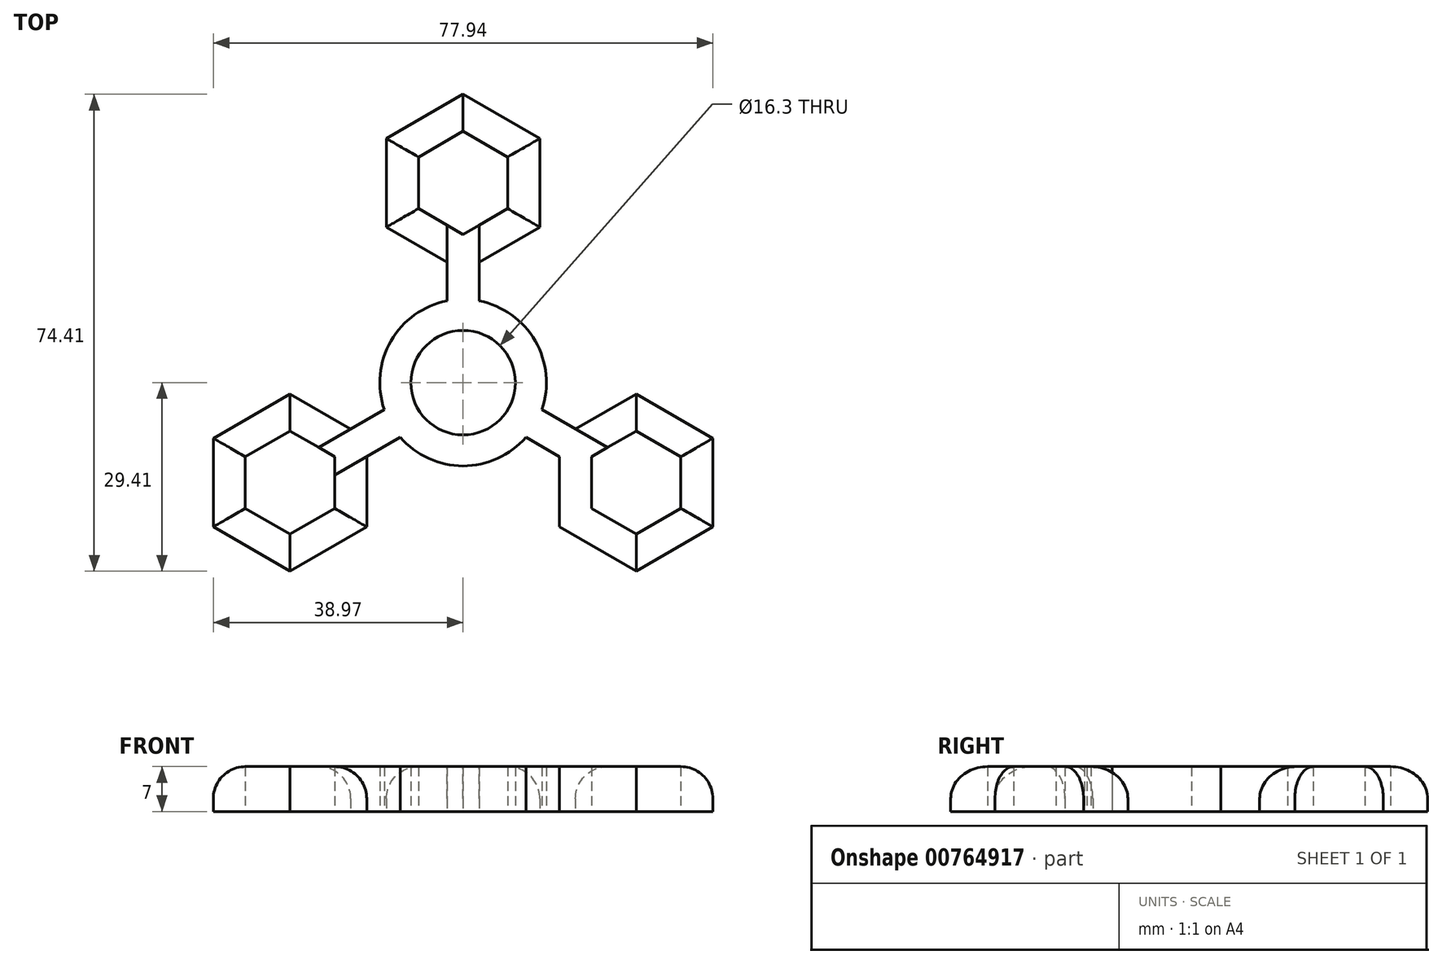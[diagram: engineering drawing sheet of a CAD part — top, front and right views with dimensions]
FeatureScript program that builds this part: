
annotation { "Feature Type Name" : "Feature", "Feature Type Description" : "" }
export const myFeature = defineFeature(function(context is Context, id is Id, definition is map)
    precondition{}
    {
        {
            var Q0;
            Q0=qCreatedBy(makeId("Top.planeOp"),FACE);
            var sketch = newSketch(context, id + "F0", { "sketchPlane" : qUnion([Q0])});
            skCircle(sketch, "E0", {"center": v(0, 0) * mm, "radius": 13 * mm});
            skLineSegment(sketch, "E1", {"start": v(-2.5, 12.76) * mm, "end": v(-2.5, 18.8) * mm});
            skLineSegment(sketch, "E2", {"start": v(2.5, 12.76) * mm, "end": v(2.5, 18.8) * mm});
            skCircle(sketch, "E3.cCircle", {"center": v(0, 31.18) * mm, "radius": 11.97 * mm, "construction": true});
            skLineSegment(sketch, "E3.0", {"start": v(-5.99, 20.8) * mm, "end": v(-11.97, 24.26) * mm});
            skLineSegment(sketch, "E3.1", {"start": v(-11.97, 24.26) * mm, "end": v(-11.97, 38.09) * mm});
            skLineSegment(sketch, "E3.2", {"start": v(-11.97, 38.09) * mm, "end": v(0, 45) * mm});
            skLineSegment(sketch, "E3.3", {"start": v(0, 45) * mm, "end": v(11.97, 38.09) * mm});
            skLineSegment(sketch, "E3.4", {"start": v(11.97, 38.09) * mm, "end": v(11.97, 24.26) * mm});
            skLineSegment(sketch, "E3.5", {"start": v(11.97, 24.26) * mm, "end": v(2.5, 18.8) * mm});
            skPoint(sketch, "E3.0.midPoint", {"position": v(-5.99, 20.8) * mm});
            skCircle(sketch, "E4.cCircle", {"center": v(0, 31.18) * mm, "radius": 6.97 * mm, "construction": true});
            skLineSegment(sketch, "E4.0", {"start": v(6.97, 35.2) * mm, "end": v(6.97, 27.15) * mm});
            skLineSegment(sketch, "E4.1", {"start": v(6.97, 27.15) * mm, "end": v(0, 23.13) * mm});
            skLineSegment(sketch, "E4.2", {"start": v(0, 23.13) * mm, "end": v(-6.97, 27.15) * mm});
            skLineSegment(sketch, "E4.3", {"start": v(-6.97, 27.15) * mm, "end": v(-6.97, 35.2) * mm});
            skLineSegment(sketch, "E4.4", {"start": v(-6.97, 35.2) * mm, "end": v(0, 39.23) * mm});
            skLineSegment(sketch, "E4.5", {"start": v(0, 39.23) * mm, "end": v(6.97, 35.2) * mm});
            skPoint(sketch, "E4.0.midPoint", {"position": v(6.97, 31.18) * mm});
            skLineSegment(sketch, "E5", {"start": v(-5.99, 20.8) * mm, "end": v(-2.5, 18.8) * mm});
            skLineSegment(sketch, "E6.1.0", {"start": v(-33.97, -11.56) * mm, "end": v(-27, -7.54) * mm});
            skPoint(sketch, "E6.1.1", {"position": v(-15.03, -15.59) * mm});
            skLineSegment(sketch, "E6.1.2", {"start": v(-20.03, -11.56) * mm, "end": v(-20.03, -19.61) * mm});
            skLineSegment(sketch, "E6.1.3", {"start": v(-27, -29.41) * mm, "end": v(-38.97, -22.5) * mm});
            skCircle(sketch, "E6.1.4", {"center": v(-27, -15.59) * mm, "radius": 11.97 * mm, "construction": true});
            skLineSegment(sketch, "E6.1.5", {"start": v(-33.97, -19.61) * mm, "end": v(-33.97, -11.56) * mm});
            skLineSegment(sketch, "E6.1.6", {"start": v(-27, -7.54) * mm, "end": v(-20.03, -11.56) * mm});
            skCircle(sketch, "E6.1.7", {"center": v(-27, -15.59) * mm, "radius": 6.97 * mm, "construction": true});
            skLineSegment(sketch, "E6.1.8", {"start": v(-27, -1.76) * mm, "end": v(-17.53, -7.23) * mm});
            skLineSegment(sketch, "E6.1.9", {"start": v(-38.97, -22.5) * mm, "end": v(-38.97, -8.68) * mm});
            skLineSegment(sketch, "E6.1.10", {"start": v(-15.03, -15.59) * mm, "end": v(-15.03, -22.5) * mm});
            skLineSegment(sketch, "E6.1.11", {"start": v(-38.97, -8.68) * mm, "end": v(-27, -1.76) * mm});
            skLineSegment(sketch, "E6.1.12", {"start": v(-15.03, -22.5) * mm, "end": v(-27, -29.41) * mm});
            skLineSegment(sketch, "E6.1.13", {"start": v(-27, -23.64) * mm, "end": v(-33.97, -19.61) * mm});
            skPoint(sketch, "E6.1.14", {"position": v(-30.49, -9.55) * mm});
            skLineSegment(sketch, "E6.1.15", {"start": v(-20.03, -19.61) * mm, "end": v(-27, -23.64) * mm});
            skLineSegment(sketch, "E6.1.16", {"start": v(-15.03, -15.59) * mm, "end": v(-15.03, -11.56) * mm});
            skLineSegment(sketch, "E6.1.17", {"start": v(-9.8, -8.54) * mm, "end": v(-15.03, -11.56) * mm});
            skLineSegment(sketch, "E6.1.18", {"start": v(-12.3, -4.21) * mm, "end": v(-17.53, -7.23) * mm});
            skLineSegment(sketch, "E6.2.0", {"start": v(27, -23.64) * mm, "end": v(20.03, -19.61) * mm});
            skPoint(sketch, "E6.2.1", {"position": v(21.01, -5.22) * mm});
            skLineSegment(sketch, "E6.2.2", {"start": v(20.03, -11.56) * mm, "end": v(27, -7.54) * mm});
            skLineSegment(sketch, "E6.2.3", {"start": v(38.97, -8.68) * mm, "end": v(38.97, -22.5) * mm});
            skCircle(sketch, "E6.2.4", {"center": v(27, -15.59) * mm, "radius": 11.97 * mm, "construction": true});
            skLineSegment(sketch, "E6.2.5", {"start": v(33.97, -19.61) * mm, "end": v(27, -23.64) * mm});
            skLineSegment(sketch, "E6.2.6", {"start": v(20.03, -19.61) * mm, "end": v(20.03, -11.56) * mm});
            skCircle(sketch, "E6.2.7", {"center": v(27, -15.59) * mm, "radius": 6.97 * mm, "construction": true});
            skLineSegment(sketch, "E6.2.8", {"start": v(15.03, -22.5) * mm, "end": v(15.03, -11.56) * mm});
            skLineSegment(sketch, "E6.2.9", {"start": v(38.97, -22.5) * mm, "end": v(27, -29.41) * mm});
            skLineSegment(sketch, "E6.2.10", {"start": v(21.01, -5.22) * mm, "end": v(27, -1.76) * mm});
            skLineSegment(sketch, "E6.2.11", {"start": v(27, -29.41) * mm, "end": v(15.03, -22.5) * mm});
            skLineSegment(sketch, "E6.2.12", {"start": v(27, -1.76) * mm, "end": v(38.97, -8.68) * mm});
            skLineSegment(sketch, "E6.2.13", {"start": v(33.97, -11.56) * mm, "end": v(33.97, -19.61) * mm});
            skPoint(sketch, "E6.2.14", {"position": v(23.51, -21.63) * mm});
            skLineSegment(sketch, "E6.2.15", {"start": v(27, -7.54) * mm, "end": v(33.97, -11.56) * mm});
            skLineSegment(sketch, "E6.2.16", {"start": v(21.01, -5.22) * mm, "end": v(17.53, -7.23) * mm});
            skLineSegment(sketch, "E6.2.17", {"start": v(12.3, -4.21) * mm, "end": v(17.53, -7.23) * mm});
            skLineSegment(sketch, "E6.2.18", {"start": v(9.8, -8.54) * mm, "end": v(15.03, -11.56) * mm});
            skCircle(sketch, "E7", {"center": v(0, 0) * mm, "radius": 8.15 * mm});
            skSolve(sketch);
        }
        {
            var Q0;
            Q0 = qSketchRegion(id + "F0", true);
            extrude(context, id + "F1", {"entities" : qUnion([Q0]), "depth" : 7 * mm, "offsetDistance" : 25 * mm});
        }
        {
            var Q0;
            Q0=makeQuery(id+"F1.opExtrude","CAP_EDGE",EDGE,{"disambiguationData":[OSD([sQuery(id+"F0.wireOp",EDGE,"E6.1.8")])],"isStart":false});
            var Q1;
            Q1=makeQuery(id+"F1.opExtrude","CAP_EDGE",EDGE,{"disambiguationData":[OSD([sQuery(id+"F0.wireOp",EDGE,"E6.1.11")])],"isStart":false});
            var Q2;
            Q2=makeQuery(id+"F1.opExtrude","CAP_EDGE",EDGE,{"disambiguationData":[OSD([sQuery(id+"F0.wireOp",EDGE,"E6.1.9")])],"isStart":false});
            var Q3;
            Q3=makeQuery(id+"F1.opExtrude","CAP_EDGE",EDGE,{"disambiguationData":[OSD([sQuery(id+"F0.wireOp",EDGE,"E6.1.3")])],"isStart":false});
            var Q4;
            Q4=makeQuery(id+"F1.opExtrude","CAP_EDGE",EDGE,{"disambiguationData":[OSD([sQuery(id+"F0.wireOp",EDGE,"E6.1.12")])],"isStart":false});
            var Q5;
            Q5=makeQuery(id+"F1.opExtrude","CAP_EDGE",EDGE,{"disambiguationData":[OSD([sQuery(id+"F0.wireOp",EDGE,"E6.1.10"),sQuery(id+"F0.wireOp",EDGE,"E6.1.16")])],"isStart":false});
            var Q6;
            Q6=makeQuery(id+"F1.opExtrude","CAP_EDGE",EDGE,{"disambiguationData":[OSD([sQuery(id+"F0.wireOp",EDGE,"E6.2.9")])],"isStart":false});
            var Q7;
            Q7=makeQuery(id+"F1.opExtrude","CAP_EDGE",EDGE,{"disambiguationData":[OSD([sQuery(id+"F0.wireOp",EDGE,"E6.2.3")])],"isStart":false});
            var Q8;
            Q8=makeQuery(id+"F1.opExtrude","CAP_EDGE",EDGE,{"disambiguationData":[OSD([sQuery(id+"F0.wireOp",EDGE,"E6.2.12")])],"isStart":false});
            var Q9;
            Q9=makeQuery(id+"F1.opExtrude","CAP_EDGE",EDGE,{"disambiguationData":[OSD([sQuery(id+"F0.wireOp",EDGE,"E6.2.10"),sQuery(id+"F0.wireOp",EDGE,"E6.2.16")])],"isStart":false});
            var Q10;
            Q10=makeQuery(id+"F1.opExtrude","CAP_EDGE",EDGE,{"disambiguationData":[OSD([sQuery(id+"F0.wireOp",EDGE,"E6.2.11")])],"isStart":false});
            var Q11;
            Q11=makeQuery(id+"F1.opExtrude","CAP_EDGE",EDGE,{"disambiguationData":[OSD([sQuery(id+"F0.wireOp",EDGE,"E3.1")])],"isStart":false});
            var Q12;
            Q12=makeQuery(id+"F1.opExtrude","CAP_EDGE",EDGE,{"disambiguationData":[OSD([sQuery(id+"F0.wireOp",EDGE,"E3.2")])],"isStart":false});
            var Q13;
            Q13=makeQuery(id+"F1.opExtrude","CAP_EDGE",EDGE,{"disambiguationData":[OSD([sQuery(id+"F0.wireOp",EDGE,"E3.3")])],"isStart":false});
            var Q14;
            Q14=makeQuery(id+"F1.opExtrude","CAP_EDGE",EDGE,{"disambiguationData":[OSD([sQuery(id+"F0.wireOp",EDGE,"E3.4")])],"isStart":false});
            var Q15;
            Q15=makeQuery(id+"F1.opExtrude","CAP_EDGE",EDGE,{"disambiguationData":[OSD([sQuery(id+"F0.wireOp",EDGE,"E3.0"),sQuery(id+"F0.wireOp",EDGE,"E5")])],"isStart":false});
            var Q16;
            Q16=makeQuery(id+"F1.opExtrude","CAP_EDGE",EDGE,{"disambiguationData":[OSD([sQuery(id+"F0.wireOp",EDGE,"E3.5")])],"isStart":false});
            var Q17;
            {var subQ0=sQuery(id+"F0.wireOp",EDGE,"E0");Q17=makeQuery(id+"F1.opExtrude","CAP_EDGE",EDGE,{"disambiguationData":[OSD([subQ0]),TDD([makeQuery(id+"F0.imprint","IMPRINT",EDGE,{"disambiguationData":[TD([[makeQuery(id+"F0.imprint","INTERSECT",VERTEX,{"derivedFrom":[subQ0,sQuery(id+"F0.wireOp",EDGE,"E1")]}),-1.0]])],"derivedFrom":subQ0})])],"isStart":false});}
            var Q18;
            {var subQ0=sQuery(id+"F0.wireOp",EDGE,"E0");Q18=makeQuery(id+"F1.opExtrude","CAP_EDGE",EDGE,{"disambiguationData":[OSD([subQ0]),TDD([makeQuery(id+"F0.imprint","IMPRINT",EDGE,{"disambiguationData":[TD([[makeQuery(id+"F0.imprint","INTERSECT",VERTEX,{"derivedFrom":[subQ0,sQuery(id+"F0.wireOp",EDGE,"E2")]}),1.0]])],"derivedFrom":subQ0})])],"isStart":false});}
            var Q19;
            {var subQ0=sQuery(id+"F0.wireOp",EDGE,"E0");Q19=makeQuery(id+"F1.opExtrude","CAP_EDGE",EDGE,{"disambiguationData":[OSD([subQ0]),TDD([makeQuery(id+"F0.imprint","IMPRINT",EDGE,{"disambiguationData":[TD([[makeQuery(id+"F0.imprint","INTERSECT",VERTEX,{"derivedFrom":[subQ0,sQuery(id+"F0.wireOp",EDGE,"E6.1.17")]}),-1.0]])],"derivedFrom":subQ0})])],"isStart":false});}
            var Q20;
            {var subQ0=sQuery(id+"F0.wireOp",EDGE,"E0");Q20=makeQuery(id+"F1.opExtrude","CAP_EDGE",EDGE,{"disambiguationData":[OSD([subQ0]),TDD([makeQuery(id+"F0.imprint","IMPRINT",EDGE,{"disambiguationData":[TD([[makeQuery(id+"F0.imprint","INTERSECT",VERTEX,{"derivedFrom":[subQ0,sQuery(id+"F0.wireOp",EDGE,"E6.1.17")]}),-1.0]])],"derivedFrom":subQ0})])],"isStart":true});}
            var Q21;
            {var subQ0=sQuery(id+"F0.wireOp",EDGE,"E0");Q21=makeQuery(id+"F1.opExtrude","CAP_EDGE",EDGE,{"disambiguationData":[OSD([subQ0]),TDD([makeQuery(id+"F0.imprint","IMPRINT",EDGE,{"disambiguationData":[TD([[makeQuery(id+"F0.imprint","INTERSECT",VERTEX,{"derivedFrom":[subQ0,sQuery(id+"F0.wireOp",EDGE,"E2")]}),1.0]])],"derivedFrom":subQ0})])],"isStart":true});}
            var Q22;
            {var subQ0=sQuery(id+"F0.wireOp",EDGE,"E0");Q22=makeQuery(id+"F1.opExtrude","CAP_EDGE",EDGE,{"disambiguationData":[OSD([subQ0]),TDD([makeQuery(id+"F0.imprint","IMPRINT",EDGE,{"disambiguationData":[TD([[makeQuery(id+"F0.imprint","INTERSECT",VERTEX,{"derivedFrom":[subQ0,sQuery(id+"F0.wireOp",EDGE,"E1")]}),-1.0]])],"derivedFrom":subQ0})])],"isStart":true});}
            fillet(context, id + "F2", {"entities" : qUnion([Q0, Q1, Q2, Q3, Q4, Q5, Q6, Q7, Q8, Q9, Q10, Q11, Q12, Q13, Q14, Q15, Q16, Q17, Q18, Q19, Q20, Q21, Q22]), "radius" : 5 * mm, "tangentPropagation" : true, "allowEdgeOverflow" : false});
        }
    });
